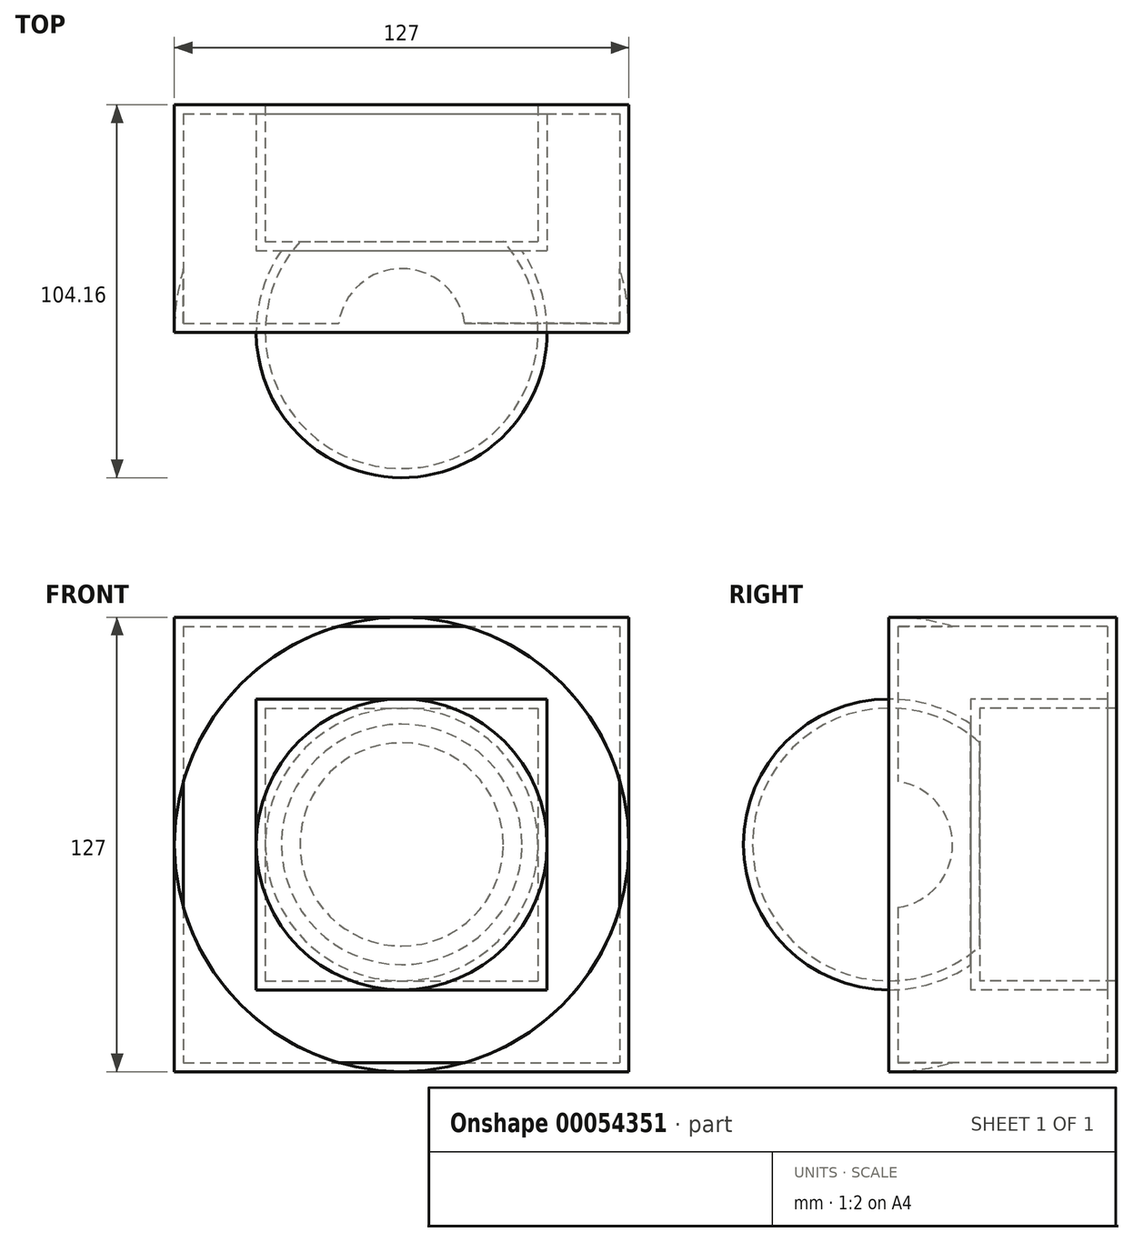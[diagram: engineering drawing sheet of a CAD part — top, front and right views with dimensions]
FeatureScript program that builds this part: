
annotation { "Feature Type Name" : "Feature", "Feature Type Description" : "" }
export const myFeature = defineFeature(function(context is Context, id is Id, definition is map)
    precondition{}
    {
        {
            var Q0;
            Q0=qCreatedBy(makeId("Front.planeOp"),FACE);
            var sketch = newSketch(context, id + "F0", { "sketchPlane" : qUnion([Q0])});
            skArc(sketch, "E0", {"start": v(0, -63.5) * mm, "mid": v(63.5, 0) * mm, "end": v(0, 63.5) * mm});
            skLineSegment(sketch, "E1", {"start": v(0, 63.5) * mm, "end": v(0, -63.5) * mm});
            skSolve(sketch);
        }
        {
            var Q0;
            Q0=makeQuery(id+"F0.imprint","IMPRINT",FACE,{"disambiguationData":[TD([[makeQuery(id+"F0.imprint","IMPRINT",EDGE,{"derivedFrom":sQuery(id+"F0.wireOp",EDGE,"E0")}),1.0]])]});
            var Q1;
            Q1=sQuery(id+"F0.wireOp",EDGE,"E1");
            revolve(context, id + "F1", {"entities" : qUnion([Q0]), "axis" : qUnion([Q1]), "revolveType" : RevolveType.ONE_DIRECTION, "angle" : 180 * degree});
        }
        {
            var Q0;
            Q0=makeQuery(id+"F1.opRevolve","CAP_FACE",FACE,{"disambiguationData":[OSD([sQuery(id+"F0.wireOp",EDGE,"E0"),sQuery(id+"F0.wireOp",EDGE,"E1")])],"isStart":true});
            var sketch = newSketch(context, id + "F2", { "sketchPlane" : qUnion([Q0])});
            skLineSegment(sketch, "E2.rect.bottom", {"start": v(63.5, 63.5) * mm, "end": v(-63.5, 63.5) * mm});
            skLineSegment(sketch, "E2.rect.top", {"start": v(63.5, -63.5) * mm, "end": v(-63.5, -63.5) * mm});
            skLineSegment(sketch, "E2.rect.left", {"start": v(63.5, 63.5) * mm, "end": v(63.5, -63.5) * mm});
            skLineSegment(sketch, "E2.rect.right", {"start": v(-63.5, 63.5) * mm, "end": v(-63.5, -63.5) * mm});
            skPoint(sketch, "E2.rect.middle", {"position": v(0, 0) * mm});
            skSolve(sketch);
        }
        {
            var Q0;
            Q0 = qSketchRegion(id + "F2", true);
            extrude(context, id + "F3", {"entities" : qUnion([Q0]), "operationType" : NewBodyOperationType.ADD, "depth" : 63.52 * mm});
        }
        {
            var Q0;
            Q0=makeQuery(id+"F3.opExtrude","CAP_FACE",FACE,{"disambiguationData":[OSD([sQuery(id+"F2.wireOp",EDGE,"E2.rect.bottom"),sQuery(id+"F2.wireOp",EDGE,"E2.rect.top"),sQuery(id+"F2.wireOp",EDGE,"E2.rect.left"),sQuery(id+"F2.wireOp",EDGE,"E2.rect.right")])],"isStart":false});
            shell(context, id + "F4", {"entities" : qUnion([Q0]), "thickness" : 25.4 * mm});
        }
        {
            var Q0;
            Q0=makeQuery(id+"F1.opRevolve","SWEPT_FACE",FACE,{"disambiguationData":[OSD([sQuery(id+"F0.wireOp",EDGE,"E0")])]});
            shell(context, id + "F5", {"entities" : qUnion([Q0]), "thickness" : 2.54 * mm});
        }
    });
